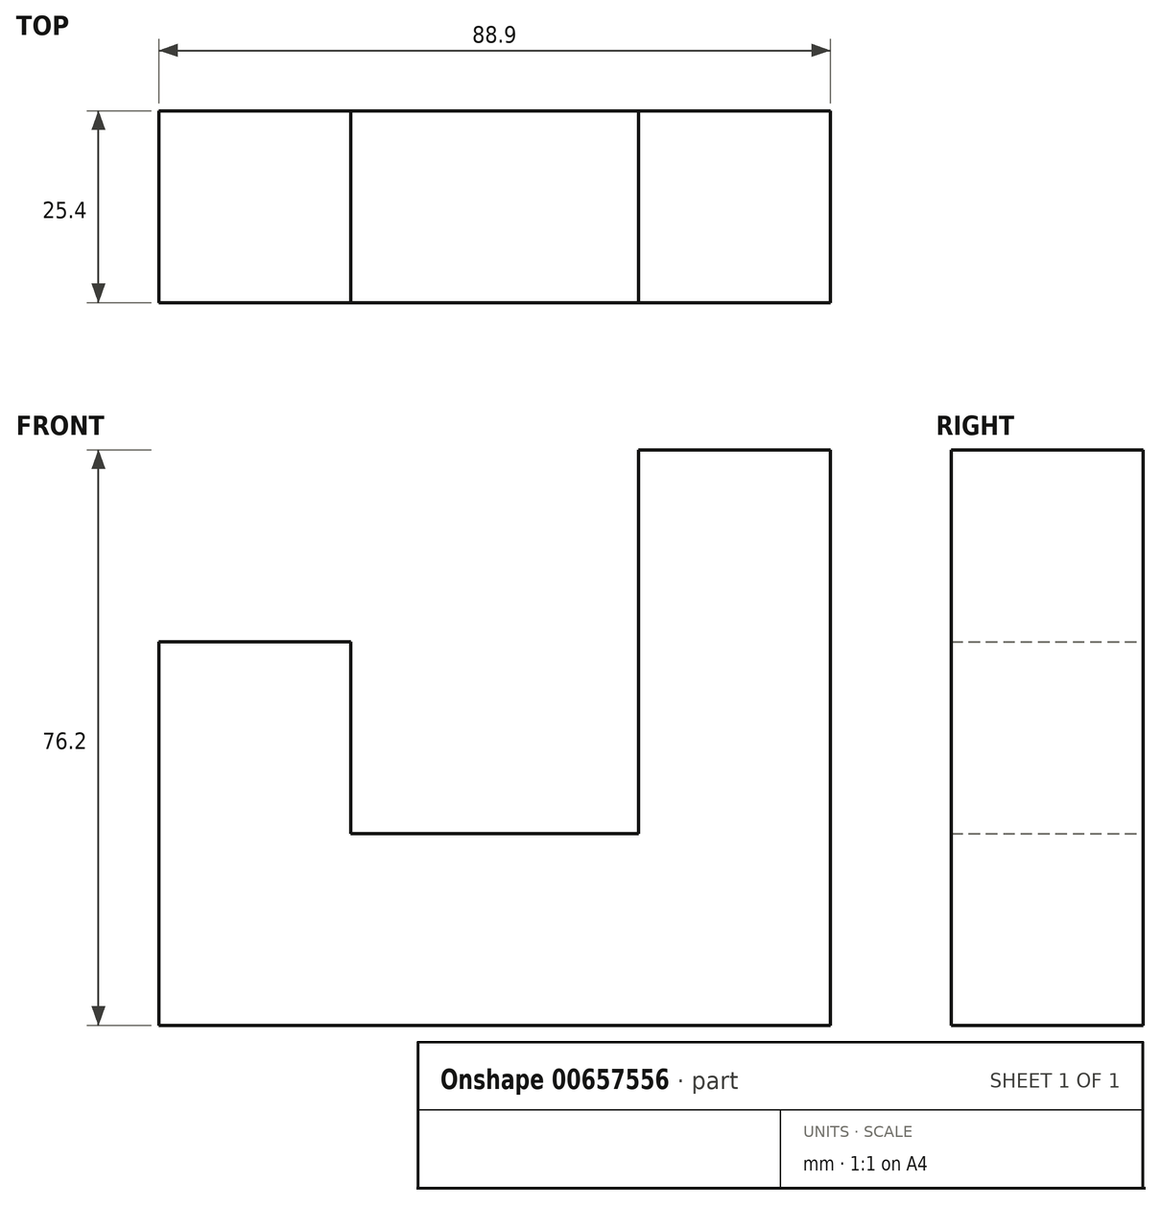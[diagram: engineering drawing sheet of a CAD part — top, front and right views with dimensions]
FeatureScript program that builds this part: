
annotation { "Feature Type Name" : "Feature", "Feature Type Description" : "" }
export const myFeature = defineFeature(function(context is Context, id is Id, definition is map)
    precondition{}
    {
        {
            var Q0;
            Q0=qCreatedBy(makeId("Front.planeOp"),FACE);
            var sketch = newSketch(context, id + "F0", { "sketchPlane" : qUnion([Q0])});
            skLineSegment(sketch, "E0", {"start": v(-49.46, -40.47) * mm, "end": v(39.44, -40.47) * mm});
            skLineSegment(sketch, "E1", {"start": v(39.44, -40.47) * mm, "end": v(39.44, 35.73) * mm});
            skLineSegment(sketch, "E2", {"start": v(39.44, 35.73) * mm, "end": v(14.04, 35.73) * mm});
            skLineSegment(sketch, "E3", {"start": v(14.04, 35.73) * mm, "end": v(14.04, -15.07) * mm});
            skLineSegment(sketch, "E4", {"start": v(14.04, -15.07) * mm, "end": v(-24.06, -15.07) * mm});
            skLineSegment(sketch, "E5", {"start": v(-24.06, -15.07) * mm, "end": v(-24.06, 10.33) * mm});
            skLineSegment(sketch, "E6", {"start": v(-24.06, 10.33) * mm, "end": v(-49.46, 10.33) * mm});
            skLineSegment(sketch, "E7", {"start": v(-49.46, 10.33) * mm, "end": v(-49.46, -40.47) * mm});
            skSolve(sketch);
        }
        {
            var Q0;
            Q0=makeQuery(id+"F0.imprint","IMPRINT",FACE,{"disambiguationData":[TD([[makeQuery(id+"F0.imprint","IMPRINT",EDGE,{"derivedFrom":sQuery(id+"F0.wireOp",EDGE,"E0")}),1.0]])]});
            extrude(context, id + "F1", {"entities" : qUnion([Q0]), "depth" : 25.4 * mm, "offsetDistance" : 25.4 * mm});
        }
    });
